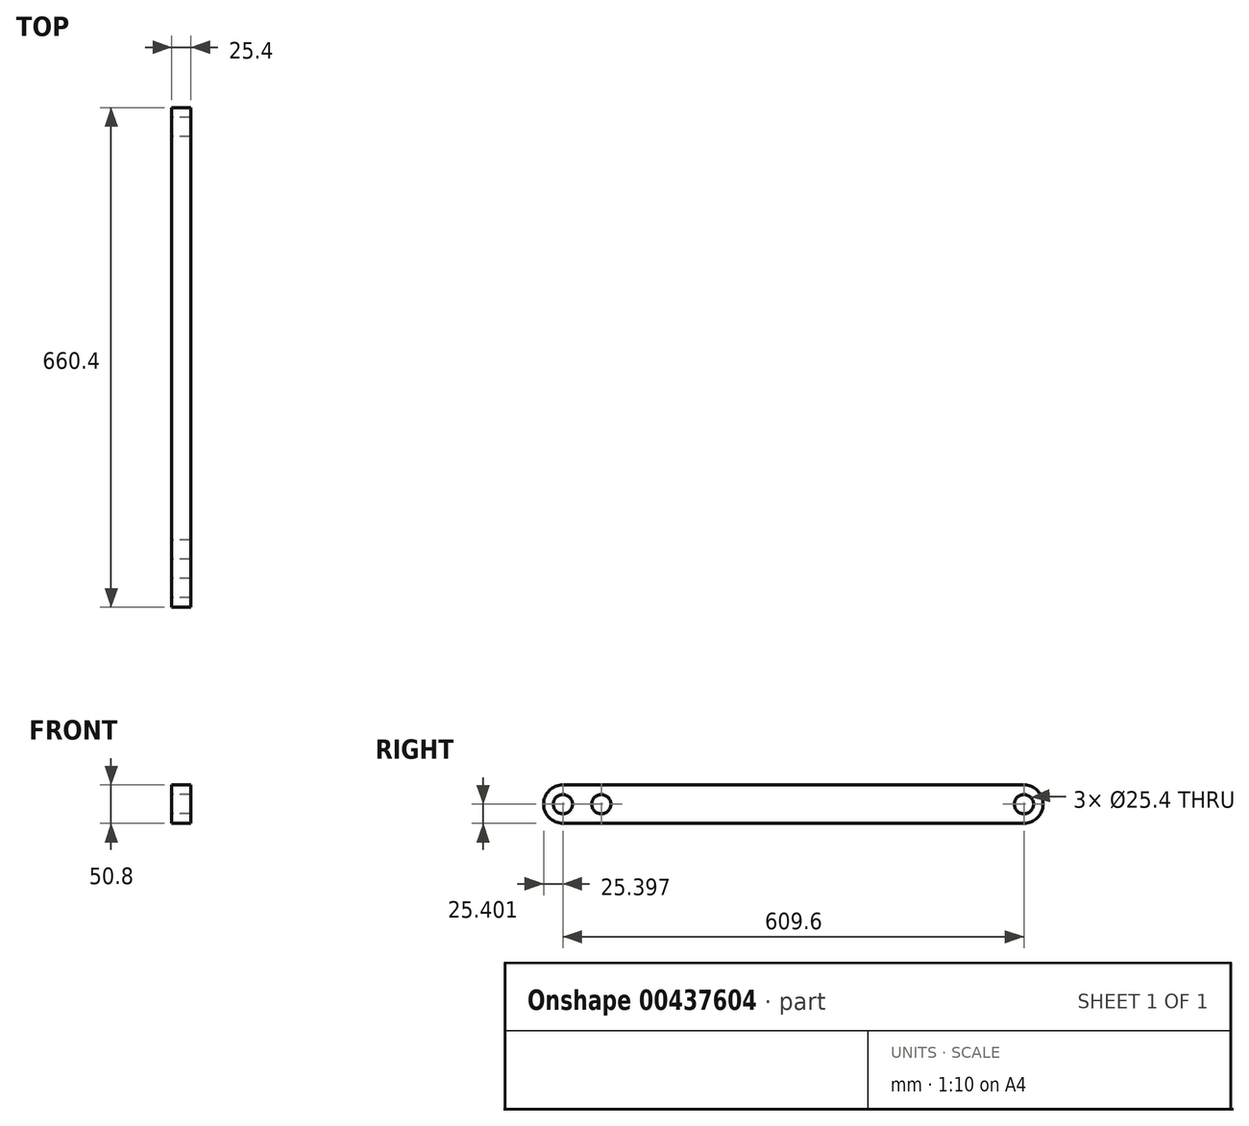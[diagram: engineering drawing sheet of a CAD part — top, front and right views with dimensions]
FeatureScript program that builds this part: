
annotation { "Feature Type Name" : "Feature", "Feature Type Description" : "" }
export const myFeature = defineFeature(function(context is Context, id is Id, definition is map)
    precondition{}
    {
        {
            var Q0;
            Q0=qCreatedBy(makeId("Right.planeOp"),FACE);
            var sketch = newSketch(context, id + "F0", { "sketchPlane" : qUnion([Q0])});
            skLineSegment(sketch, "E0.bottom", {"start": v(-265.08, 4.3) * mm, "end": v(344.52, 4.3) * mm});
            skLineSegment(sketch, "E0.top", {"start": v(-265.08, -46.5) * mm, "end": v(344.52, -46.5) * mm});
            skLineSegment(sketch, "E0.left", {"start": v(-265.08, 4.3) * mm, "end": v(-265.08, -46.5) * mm});
            skLineSegment(sketch, "E0.right", {"start": v(344.52, 4.3) * mm, "end": v(344.52, -46.5) * mm});
            skCircle(sketch, "E1", {"center": v(-265.08, -21.1) * mm, "radius": 25.4 * mm});
            skCircle(sketch, "E2", {"center": v(-265.08, -21.1) * mm, "radius": 12.7 * mm});
            skCircle(sketch, "E3", {"center": v(344.52, -21.1) * mm, "radius": 25.4 * mm});
            skCircle(sketch, "E4", {"center": v(344.52, -21.1) * mm, "radius": 12.7 * mm});
            skLineSegment(sketch, "E5", {"start": v(-239.68, -21.1) * mm, "end": v(-214.28, -21.1) * mm});
            skCircle(sketch, "E6", {"center": v(-214.28, -21.1) * mm, "radius": 12.7 * mm});
            skSolve(sketch);
        }
        {
            var Q0;
            Q0 = qSketchRegion(id + "F0", true);
            extrude(context, id + "F1", {"entities" : qUnion([Q0]), "depth" : 25.4 * mm});
        }
    });
